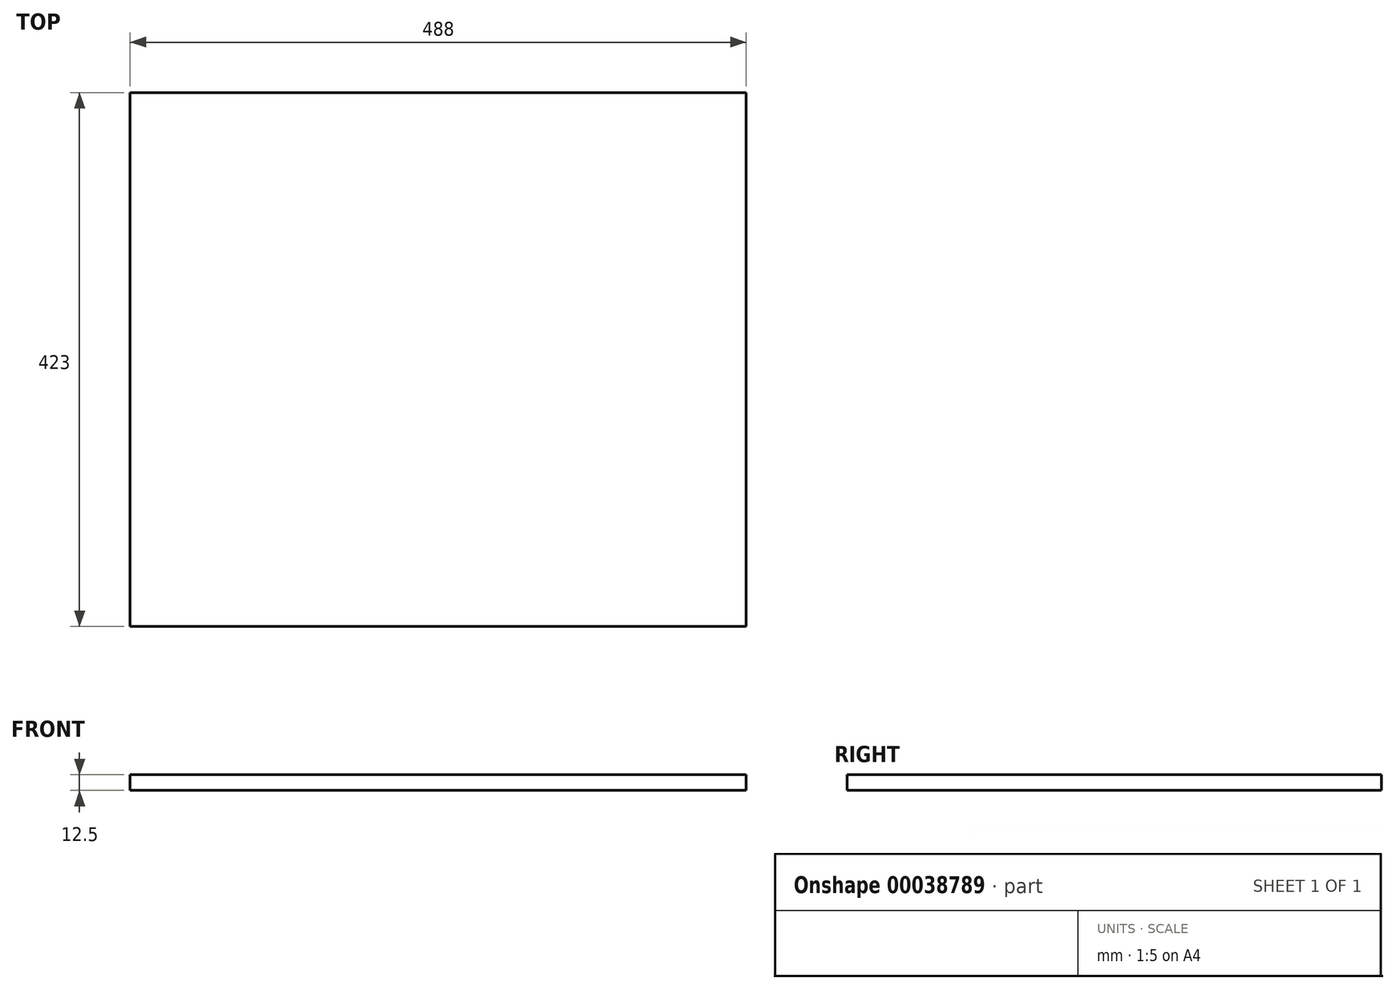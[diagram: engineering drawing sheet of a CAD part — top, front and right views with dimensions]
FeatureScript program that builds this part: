
annotation { "Feature Type Name" : "Feature", "Feature Type Description" : "" }
export const myFeature = defineFeature(function(context is Context, id is Id, definition is map)
    precondition{}
    {
        {
            var Q0;
            Q0=qCreatedBy(makeId("Top.planeOp"),FACE);
            var sketch = newSketch(context, id + "F0", { "sketchPlane" : qUnion([Q0])});
            skLineSegment(sketch, "E0.bottom", {"start": v(-70.96, 65.05) * mm, "end": v(417.04, 65.05) * mm});
            skLineSegment(sketch, "E0.top", {"start": v(-70.96, -357.95) * mm, "end": v(417.04, -357.95) * mm});
            skLineSegment(sketch, "E0.left", {"start": v(-70.96, 65.05) * mm, "end": v(-70.96, -357.95) * mm});
            skLineSegment(sketch, "E0.right", {"start": v(417.04, 65.05) * mm, "end": v(417.04, -357.95) * mm});
            skSolve(sketch);
        }
        {
            var Q0;
            Q0=qSketchRegion(id+"F0",true);
            extrude(context, id + "F1", {"entities" : qUnion([Q0]), "depth" : 12.5 * mm});
        }
    });
